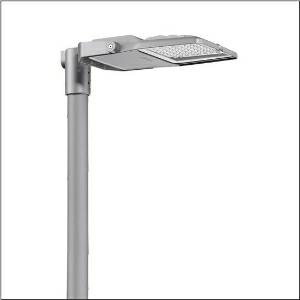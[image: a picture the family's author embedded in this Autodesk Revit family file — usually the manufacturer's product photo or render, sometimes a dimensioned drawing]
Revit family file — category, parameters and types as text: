
# Revit family: floodlight_fl_21_mini___pl52_5xa7771b4d3a_a4d9
name_source: partatom
category: Lighting Fixtures
units: mm (PartAtom-declared; Revit-internal decimal feet)

## family parameters
Cut with Voids When Loaded = No
Host = Face
Light Source = No
Part Type = Normal
Room Calculation Point = No
Round Connector Dimension = Use Diameter
Shared = No

## types (1)
- --- (1 x LED, 6490 lm, 45.5 W, 4000K)
    Apparent Load = 46 VA
    CIE Flux Codes = 26 60 98 100 100
    Color Rendering = 70
    Color Temperature = 4000K
    Default Elevation = 1800 mm
    Description = Floodlight FL 21 mini, floodlight, primary light control with lens, of PMMA, primary optical cover: protective disc, of toughened safety glass, transparent, light distribution: PL52, light emission: direct distribution, installation type: surface-mounted, LED, High Power LED, rated luminous flux: 6.490lm, luminous efficacy: 143lm/W, light colour: 740, colour temperature: 4000K, control gear: ECG iQ, control: Auto-Match, Temp-Guard, Lumen-Switch, Night-Set, Smart-Wire, Light-Fading, Desk-Remote (wireless, voltage-free reading and setting of iQ features in the workshop via application-optimized NFC function/RFID function), optimised constant luminous flux control (CLO 2.0), with terminal, 6-pole, mains connection: 220..240V, AC, 50/60Hz, start of lifetime: 46W, end of lifetime: 48W, reduction: 22W, luminaire housing, of diecast aluminium, powder-coated, Siteco® metallic grey (DB 702S), corrosivity category C5 according to DIN EN ISO 12944, mast bracket, of steel, galvanised, powder-coated, Siteco® metallic grey (DB 702S), protection rating (complete): IP66, insulation class (complete): insulation class II (safety insulation), certification: CE, ENEC, VDE, protection symbol: D, impact resistance: IK08, permissible operating ambient temperature: -40..+40°C, permissible operating ambient temperature for outdoor applications: -40..+50°C, standard: DIN EN 12944, packaging unit: 1 piece

Light Distribution: PL52
    Height = 70 mm
    Lamp = 1 x LED
    Lamp Light Flux = 6490 lm
    Lamp Power = 45.5 W
    Lamp count = 1
    Length = 485 mm
    Luminous efficacy = 143 lm/W
    Manufacturer = Siteco
    ModVariant = No
    Model = 5XA7771B4D3A
    Number of Poles = 1
    OnlyDefault = Yes
    Power Factor = 1
    Product Name = Floodlight FL 21 mini | PL52
    Product group = floodlight | pylon top
    ProductGroupID = 6101
    Protection Class = Protection class II
    Protection Degree = IP 66
    RLX_Detail_Level = 1
    RlxData = <blob elided: 101249 chars, md5=b51f85a1>
    Socket = socket
    Standby Power = 0 W
    System Light Flux = 6490 lm
    System Power = 46 W
    Type Comments = factory setting: luminous flux: 100 % | dim-lin: 254 | 463 mA
    Type Image = l_1007125.jpg
    URL = http://relux.com
    VarID = @adj_076107
    Voltage = 0 V
    Weight = 0.00 kg
    Width = 337 mm

## geometry (parser evidence)
native form markers: Blend x4, Sweep x11
no freeform markers — native parametric forms only
